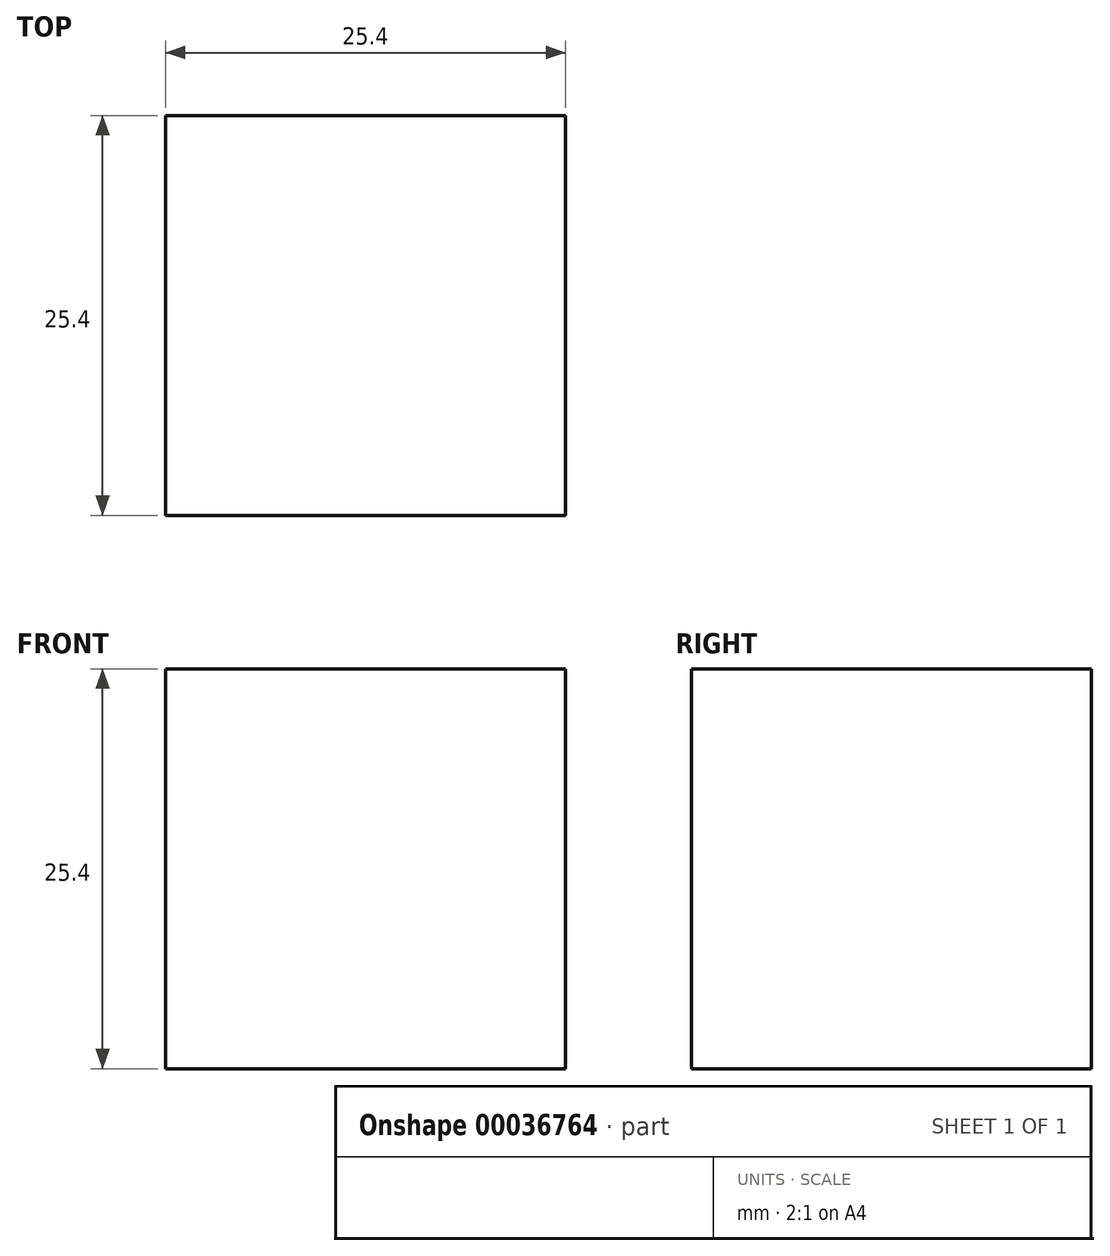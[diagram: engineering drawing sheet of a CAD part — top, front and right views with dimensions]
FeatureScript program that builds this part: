
annotation { "Feature Type Name" : "Feature", "Feature Type Description" : "" }
export const myFeature = defineFeature(function(context is Context, id is Id, definition is map)
    precondition{}
    {
        {
            var Q0;
            Q0=qCreatedBy(makeId("Front.planeOp"),FACE);
            var sketch = newSketch(context, id + "F0", { "sketchPlane" : qUnion([Q0])});
            skLineSegment(sketch, "E0.bottom", {"start": v(0, 0) * mm, "end": v(25.4, 0) * mm});
            skLineSegment(sketch, "E0.top", {"start": v(0, -25.4) * mm, "end": v(25.4, -25.4) * mm});
            skLineSegment(sketch, "E0.left", {"start": v(0, 0) * mm, "end": v(0, -25.4) * mm});
            skLineSegment(sketch, "E0.right", {"start": v(25.4, 0) * mm, "end": v(25.4, -25.4) * mm});
            skSolve(sketch);
        }
        {
            var Q0;
            Q0=makeQuery(id+"F0.imprint","IMPRINT",FACE,{"disambiguationData":[TD([[makeQuery(id+"F0.imprint","IMPRINT",EDGE,{"derivedFrom":sQuery(id+"F0.wireOp",EDGE,"E0.bottom")}),-1.0]])]});
            extrude(context, id + "F1", {"entities" : qUnion([Q0]), "depth" : 25.4 * mm});
        }
    });
